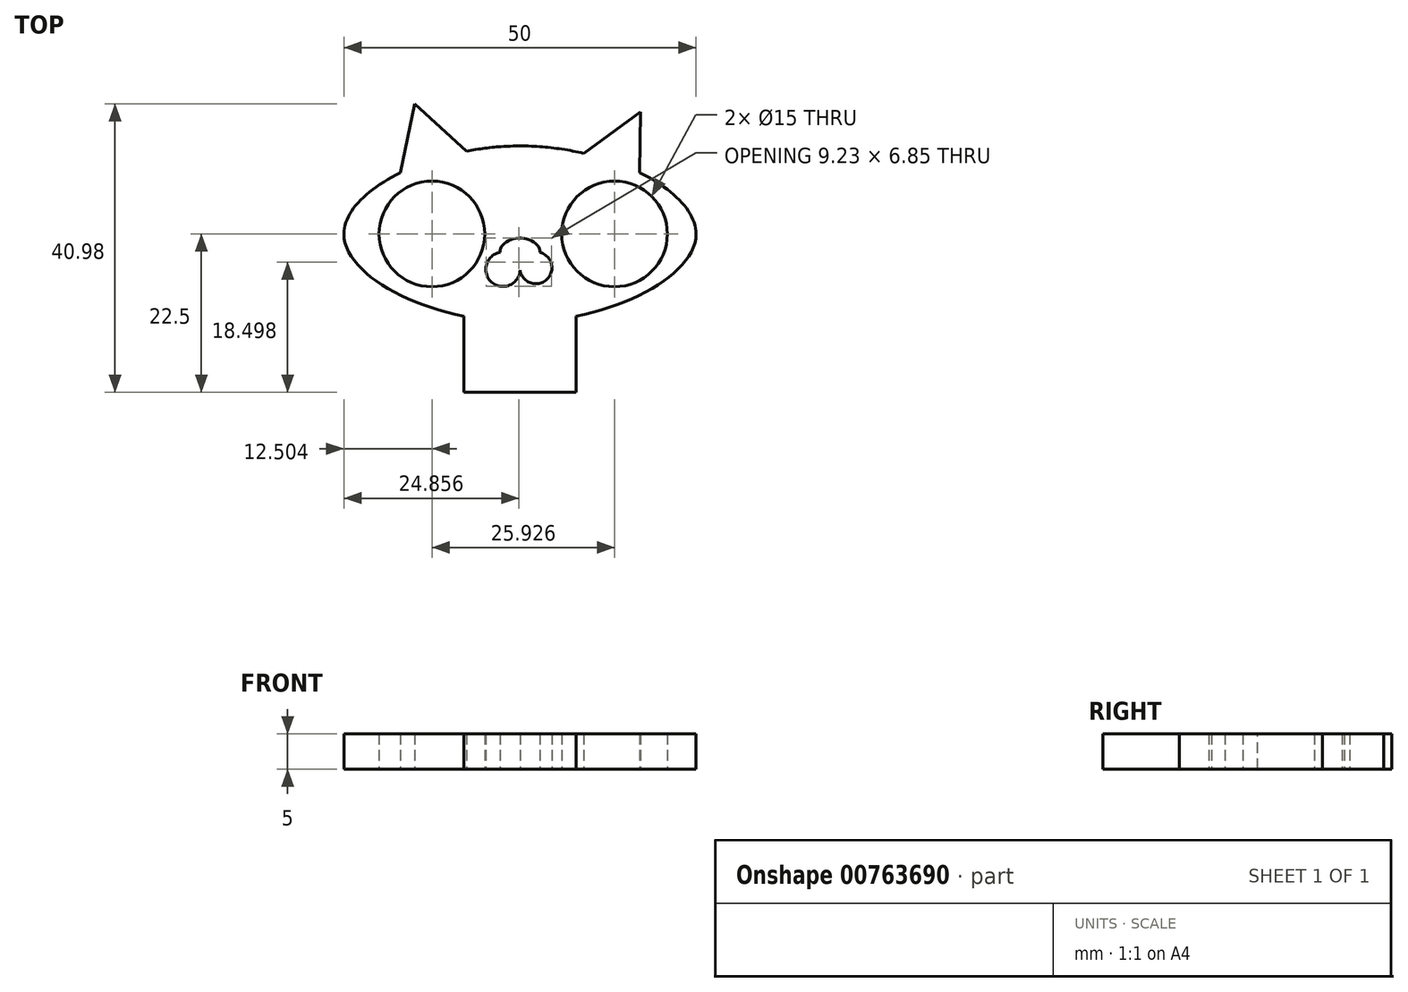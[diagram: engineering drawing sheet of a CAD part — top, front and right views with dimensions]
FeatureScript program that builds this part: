
annotation { "Feature Type Name" : "Feature", "Feature Type Description" : "" }
export const myFeature = defineFeature(function(context is Context, id is Id, definition is map)
    precondition{}
    {
        {
            var Q0;
            Q0=qCreatedBy(makeId("Top.planeOp"),FACE);
            var sketch = newSketch(context, id + "F0", { "sketchPlane" : qUnion([Q0])});
            skCircle(sketch, "E0", {"center": v(-38.4, 0) * mm, "radius": 7.5 * mm});
            skCircle(sketch, "E1", {"center": v(-12.48, 0) * mm, "radius": 7.5 * mm});
            skPoint(sketch, "E2.start.orphan", {"position": v(-30.9, 0) * mm});
            skLineSegment(sketch, "E3", {"start": v(-30.9, 0) * mm, "end": v(-25.9, 0) * mm});
            skLineSegment(sketch, "E4", {"start": v(-25.9, 0) * mm, "end": v(-25.9, 12.5) * mm});
            skLineSegment(sketch, "E5", {"start": v(-25.9, 0) * mm, "end": v(-25.9, -12.5) * mm});
            skLineSegment(sketch, "E6", {"start": v(-25.9, 0) * mm, "end": v(-0.9, 0) * mm});
            skLineSegment(sketch, "E7", {"start": v(-25.9, 0) * mm, "end": v(-50.9, 0) * mm});
            skPoint(sketch, "E7.endSnap0", {"position": v(-28.4, 0) * mm});
            skFitSpline(sketch, "E8", {"points": [v(-25.9, -12.5) * mm, v(-50.9, 0) * mm, v(-25.9, 12.5) * mm, v(-0.9, 0) * mm, v(-25.9, -12.5) * mm]});
            skEllipse(sketch, "E9", {"center": v(-25.9, -2.62) * mm, "majorRadius": 2.84 * mm, "minorRadius": 2.04 * mm, "majorAxis": v(1, 0)});
            skArc(sketch, "E10", {"start": v(-28.75, -2.62) * mm, "mid": v(-29.74, -7) * mm, "end": v(-25.9, -4.65) * mm});
            skArc(sketch, "E11", {"start": v(-25.9, -4.65) * mm, "mid": v(-22.32, -6.65) * mm, "end": v(-23.06, -2.62) * mm});
            skPoint(sketch, "E11.midSnap0", {"position": v(-23.06, -2.62) * mm});
            skPoint(sketch, "E11.midSnap1", {"position": v(-29.74, -7) * mm});
            skLineSegment(sketch, "E12", {"start": v(-25.9, 8.69) * mm, "end": v(-42.9, 8.69) * mm});
            skLineSegment(sketch, "E13", {"start": v(-25.9, 8.69) * mm, "end": v(-8.9, 8.69) * mm});
            skLineSegment(sketch, "E14", {"start": v(-42.9, 8.69) * mm, "end": v(-40.89, 18.48) * mm});
            skLineSegment(sketch, "E15", {"start": v(-40.89, 18.48) * mm, "end": v(-33.48, 11.77) * mm});
            skLineSegment(sketch, "E16", {"start": v(-8.9, 7.34) * mm, "end": v(-8.78, 17.34) * mm});
            skLineSegment(sketch, "E17", {"start": v(-8.78, 17.34) * mm, "end": v(-16.87, 11.46) * mm});
            skLineSegment(sketch, "E18", {"start": v(-40.89, 18.48) * mm, "end": v(-41.15, 9.48) * mm});
            skLineSegment(sketch, "E19", {"start": v(-8.78, 17.34) * mm, "end": v(-15.2, 11.04) * mm});
            skLineSegment(sketch, "E20", {"start": v(-25.9, -12.5) * mm, "end": v(-25.9, -22.5) * mm});
            skLineSegment(sketch, "E21", {"start": v(-25.9, -22.5) * mm, "end": v(-33.9, -22.5) * mm});
            skLineSegment(sketch, "E22", {"start": v(-33.9, -22.5) * mm, "end": v(-33.9, -11.68) * mm});
            skLineSegment(sketch, "E23", {"start": v(-25.9, -22.5) * mm, "end": v(-17.9, -22.5) * mm});
            skLineSegment(sketch, "E24", {"start": v(-17.9, -22.5) * mm, "end": v(-17.9, -11.68) * mm});
            skSolve(sketch);
        }
        {
            var Q0;
            Q0 = qSketchRegion(id + "F0", true);
            extrude(context, id + "F1", {"entities" : qUnion([Q0]), "depth" : 5 * mm, "offsetDistance" : 25 * mm});
        }
    });
